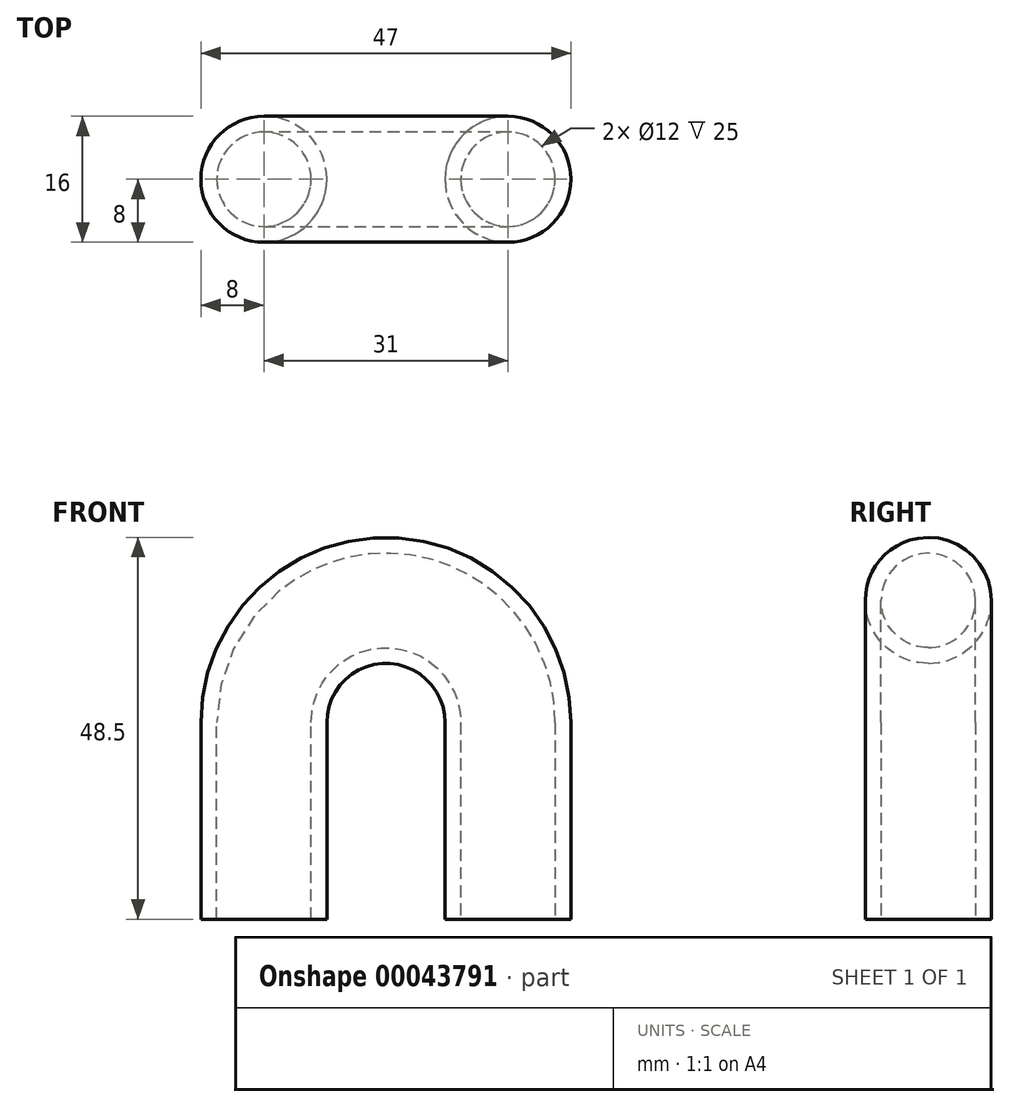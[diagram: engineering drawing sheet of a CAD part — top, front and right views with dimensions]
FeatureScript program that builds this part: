
annotation { "Feature Type Name" : "Feature", "Feature Type Description" : "" }
export const myFeature = defineFeature(function(context is Context, id is Id, definition is map)
    precondition{}
    {
        {
            var Q0;
            Q0=qCreatedBy(makeId("Front.planeOp"),FACE);
            var sketch = newSketch(context, id + "F0", { "sketchPlane" : qUnion([Q0])});
            skLineSegment(sketch, "E0", {"start": v(-15.5, 0) * mm, "end": v(-15.5, 25) * mm});
            skArc(sketch, "E1", {"start": v(0, 40.5) * mm, "mid": v(-10.96, 35.96) * mm, "end": v(-15.5, 25) * mm});
            skArc(sketch, "E2.MirrorCS", {"start": v(0, 40.5) * mm, "mid": v(10.96, 35.96) * mm, "end": v(15.5, 25) * mm});
            skLineSegment(sketch, "E3.MirrorCS", {"start": v(15.5, 0) * mm, "end": v(15.5, 25) * mm});
            skLineSegment(sketch, "E4", {"start": v(-23.5, 14.67) * mm, "end": v(-7.5, 14.67) * mm});
            skLineSegment(sketch, "E5.MirrorCS", {"start": v(23.5, 14.67) * mm, "end": v(7.5, 14.67) * mm});
            skSolve(sketch);
        }
        {
            var Q0;
            Q0=qCreatedBy(makeId("Top.planeOp"),FACE);
            var sketch = newSketch(context, id + "F1", { "sketchPlane" : qUnion([Q0])});
            skPoint(sketch, "E6.0", {"position": v(-15.5, 0) * mm});
            skCircle(sketch, "E7", {"center": v(-15.5, 0) * mm, "radius": 8 * mm});
            skCircle(sketch, "E8.0", {"center": v(-15.5, 0) * mm, "radius": 6 * mm});
            skSolve(sketch);
        }
        {
            var Q0;
            Q0=makeQuery(id+"F1.imprint","IMPRINT",FACE,{"disambiguationData":[TD([[makeQuery(id+"F1.imprint","IMPRINT",EDGE,{"derivedFrom":sQuery(id+"F1.wireOp",EDGE,"E7")}),1.0]])]});
            var Q1;
            Q1=sQuery(id+"F0.wireOp",EDGE,"E0");
            var Q2;
            Q2=sQuery(id+"F0.wireOp",EDGE,"E1");
            var Q3;
            Q3=sQuery(id+"F0.wireOp",EDGE,"E2.MirrorCS");
            var Q4;
            Q4=sQuery(id+"F0.wireOp",EDGE,"E3.MirrorCS");
            sweep(context, id + "F2", {"profiles" : qUnion([Q0]), "path" : qUnion([Q1, Q2, Q3, Q4])});
        }
    });
